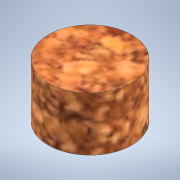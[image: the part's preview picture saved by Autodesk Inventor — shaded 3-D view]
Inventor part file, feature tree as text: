
AUTODESK INVENTOR PART (.ipt)
format: ipt  version: 2021 (Build 250183000, 183)  size: 133,120 bytes
history: native  units: mm
features: revolve x1, sketch x1
ambient origin geometry x8: Origin, YZ Plane, XZ Plane, XY Plane, X Axis, Y Axis, Z Axis, Center Point
bodies: Solid1 (feature_tree)
feature tree (2):
  revolve  "Revolution1"  [1 undecoded]
  sketch  "Sketch1"  dims[d0=20.0mm d1=15.5mm d2=90.0deg]
note: 1 required parameter value undecoded (feature->parameter linkage not recoverable at this tier; creation-order binding heuristic only, values carry confidence <= 0.55)
